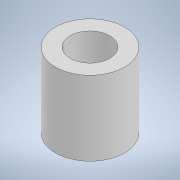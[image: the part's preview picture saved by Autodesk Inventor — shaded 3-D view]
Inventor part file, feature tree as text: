
AUTODESK INVENTOR PART (.ipt)
format: ipt  version: 2022.3 (Build 263350000, 350)  size: 98,304 bytes
history: native  units: mm
features: extrude x1, sketch x1
ambient origin geometry x8: Origin, YZ Plane, XZ Plane, XY Plane, X Axis, Y Axis, Z Axis, Center Point
bodies: Solid1 (feature_tree)
feature tree (2):
  extrude  "Extrusion1"  Depth=10.0mm
  sketch  "Sketch1"  dims[d0=5.3mm d1=2.0mm d2=10.0mm d3=0.0mm]
